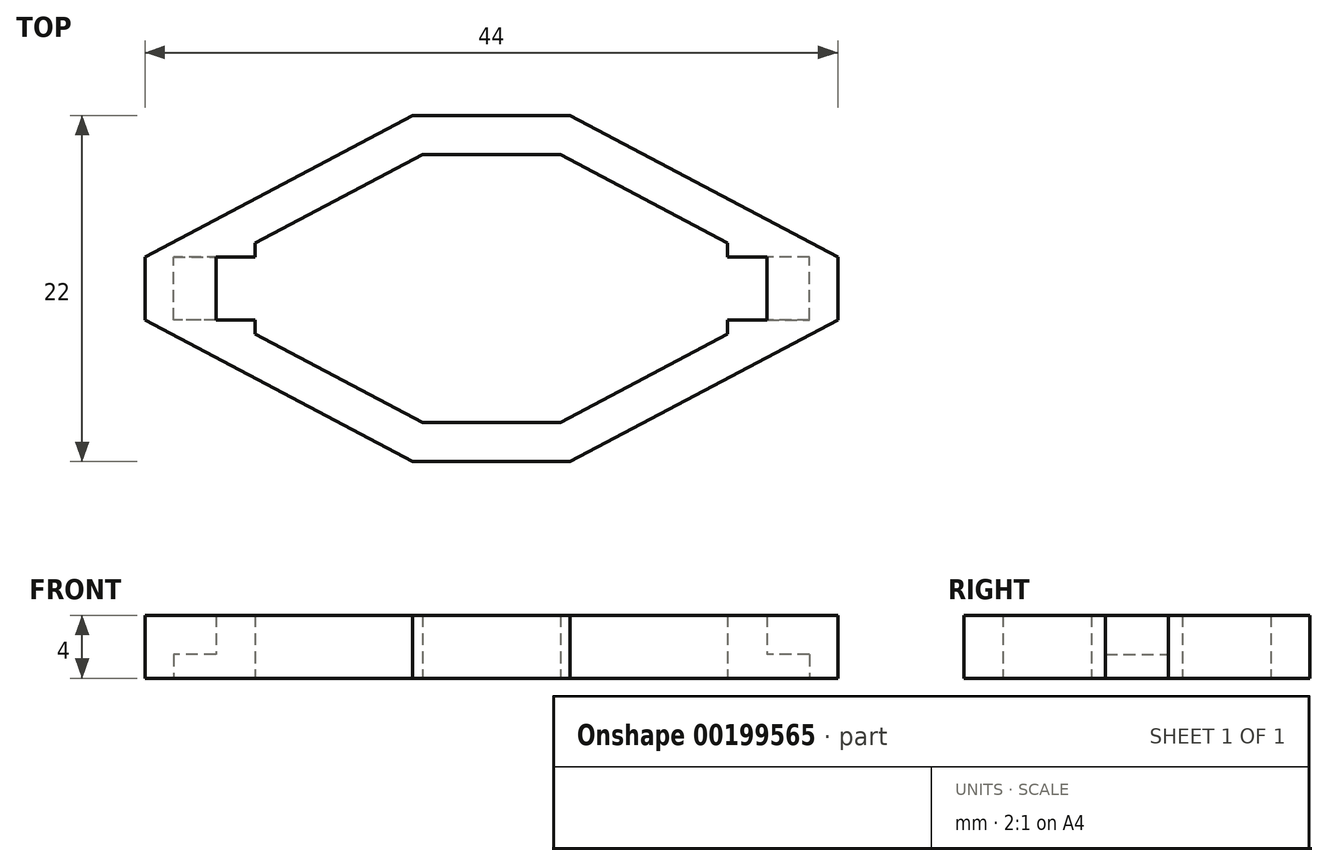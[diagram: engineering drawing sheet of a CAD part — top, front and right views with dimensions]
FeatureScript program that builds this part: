
annotation { "Feature Type Name" : "Feature", "Feature Type Description" : "" }
export const myFeature = defineFeature(function(context is Context, id is Id, definition is map)
    precondition{}
    {
        {
            var Q0;
            Q0=qCreatedBy(makeId("Top.planeOp"),FACE);
            var sketch = newSketch(context, id + "F0", { "sketchPlane" : qUnion([Q0])});
            skLineSegment(sketch, "E0.bottom", {"start": v(5, -11) * mm, "end": v(-5, -11) * mm});
            skLineSegment(sketch, "E0.top", {"start": v(5, 11) * mm, "end": v(-5, 11) * mm});
            skLineSegment(sketch, "E0.left", {"start": v(22, -2) * mm, "end": v(22, 2) * mm});
            skLineSegment(sketch, "E0.right", {"start": v(-22, -2) * mm, "end": v(-22, 2) * mm});
            skPoint(sketch, "E0.middle", {"position": v(0, 0) * mm});
            skLineSegment(sketch, "E1.bottom", {"start": v(4.38, -8.5) * mm, "end": v(-4.38, -8.5) * mm});
            skLineSegment(sketch, "E1.left", {"start": v(17.5, -2) * mm, "end": v(17.5, 2) * mm});
            skLineSegment(sketch, "E1.right", {"start": v(-17.5, -2) * mm, "end": v(-17.5, 2) * mm});
            skLineSegment(sketch, "E2.bottom", {"start": v(17.5, -2) * mm, "end": v(15, -2) * mm});
            skLineSegment(sketch, "E2.top", {"start": v(17.5, 2) * mm, "end": v(15, 2) * mm});
            skLineSegment(sketch, "E3", {"start": v(-22, 2) * mm, "end": v(-5, 11) * mm});
            skLineSegment(sketch, "E4", {"start": v(5, 11) * mm, "end": v(22, 2) * mm});
            skLineSegment(sketch, "E5", {"start": v(-22, -2) * mm, "end": v(-5, -11) * mm});
            skLineSegment(sketch, "E6", {"start": v(5, -11) * mm, "end": v(22, -2) * mm});
            skLineSegment(sketch, "E7", {"start": v(-15, 2.88) * mm, "end": v(-15, 2) * mm});
            skLineSegment(sketch, "E8", {"start": v(15, 2.88) * mm, "end": v(15, 2) * mm});
            skLineSegment(sketch, "E9.trimOffspring", {"start": v(4.38, 8.5) * mm, "end": v(-4.38, 8.5) * mm});
            skLineSegment(sketch, "E10.1", {"start": v(-15, -2.88) * mm, "end": v(-4.38, -8.5) * mm});
            skLineSegment(sketch, "E10.2", {"start": v(-15, 2.88) * mm, "end": v(-4.38, 8.5) * mm});
            skLineSegment(sketch, "E10.5", {"start": v(4.38, 8.5) * mm, "end": v(15, 2.88) * mm});
            skLineSegment(sketch, "E10.7", {"start": v(4.38, -8.5) * mm, "end": v(15, -2.88) * mm});
            skLineSegment(sketch, "E11.trimOffspring", {"start": v(-15, 2) * mm, "end": v(-17.5, 2) * mm});
            skLineSegment(sketch, "E12.trimOffspring", {"start": v(-15, -2) * mm, "end": v(-15, -2.88) * mm});
            skLineSegment(sketch, "E13.trimOffspring", {"start": v(-15, -2) * mm, "end": v(-17.5, -2) * mm});
            skLineSegment(sketch, "E14.trimOffspring", {"start": v(15, -2) * mm, "end": v(15, -2.88) * mm});
            skPoint(sketch, "E15", {"position": v(-22, 2) * mm});
            skPoint(sketch, "E16", {"position": v(-17.5, 2) * mm});
            skPoint(sketch, "E17", {"position": v(-17.5, -2) * mm});
            skPoint(sketch, "E18", {"position": v(-22, -2) * mm});
            skPoint(sketch, "E19", {"position": v(17.5, 2) * mm});
            skPoint(sketch, "E20", {"position": v(22, 2) * mm});
            skPoint(sketch, "E21", {"position": v(17.5, -2) * mm});
            skPoint(sketch, "E22", {"position": v(22, -2) * mm});
            skSolve(sketch);
        }
        {
            var Q0;
            Q0=makeQuery(id+"F0.imprint","IMPRINT",FACE,{"disambiguationData":[TD([[makeQuery(id+"F0.imprint","IMPRINT",EDGE,{"derivedFrom":sQuery(id+"F0.wireOp",EDGE,"E1.left")}),-1.0]])]});
            extrude(context, id + "F1", {"entities" : qUnion([Q0]), "depth" : 4 * mm});
        }
        {
            var Q0;
            Q0=makeQuery(id+"F1.opExtrude","CAP_FACE",FACE,{"disambiguationData":[OSD([sQuery(id+"F0.wireOp",EDGE,"E1.left"),sQuery(id+"F0.wireOp",EDGE,"E1.right"),sQuery(id+"F0.wireOp",EDGE,"E2.bottom"),sQuery(id+"F0.wireOp",EDGE,"E2.top"),sQuery(id+"F0.wireOp",EDGE,"E0.left"),sQuery(id+"F0.wireOp",EDGE,"E0.right"),sQuery(id+"F0.wireOp",EDGE,"E0.bottom"),sQuery(id+"F0.wireOp",EDGE,"E0.top"),sQuery(id+"F0.wireOp",EDGE,"E3"),sQuery(id+"F0.wireOp",EDGE,"E4"),sQuery(id+"F0.wireOp",EDGE,"E5"),sQuery(id+"F0.wireOp",EDGE,"E6"),sQuery(id+"F0.wireOp",EDGE,"E7"),sQuery(id+"F0.wireOp",EDGE,"E8"),sQuery(id+"F0.wireOp",EDGE,"E10.1"),sQuery(id+"F0.wireOp",EDGE,"E10.2"),sQuery(id+"F0.wireOp",EDGE,"E1.bottom"),sQuery(id+"F0.wireOp",EDGE,"E9.trimOffspring"),sQuery(id+"F0.wireOp",EDGE,"E10.5"),sQuery(id+"F0.wireOp",EDGE,"E10.7"),sQuery(id+"F0.wireOp",EDGE,"E11.trimOffspring"),sQuery(id+"F0.wireOp",EDGE,"E12.trimOffspring"),sQuery(id+"F0.wireOp",EDGE,"E13.trimOffspring"),sQuery(id+"F0.wireOp",EDGE,"E14.trimOffspring")])],"isStart":true});
            var sketch = newSketch(context, id + "F2", { "sketchPlane" : qUnion([Q0])});
            skLineSegment(sketch, "E23", {"start": v(-17.5, 2) * mm, "end": v(-22, 2) * mm});
            skLineSegment(sketch, "E24", {"start": v(-22, 2) * mm, "end": v(-22, -2) * mm});
            skLineSegment(sketch, "E25", {"start": v(-22, -2) * mm, "end": v(-17.5, -2) * mm});
            skLineSegment(sketch, "E26", {"start": v(-17.5, -2) * mm, "end": v(-17.5, 2) * mm});
            skLineSegment(sketch, "E27", {"start": v(17.5, 2) * mm, "end": v(22, 2) * mm});
            skLineSegment(sketch, "E28", {"start": v(22, 2) * mm, "end": v(22, -2) * mm});
            skLineSegment(sketch, "E29", {"start": v(22, -2) * mm, "end": v(17.5, -2) * mm});
            skLineSegment(sketch, "E30", {"start": v(17.5, -2) * mm, "end": v(17.5, 2) * mm});
            skLineSegment(sketch, "E31", {"start": v(-20.2, 2) * mm, "end": v(-20.2, -2) * mm});
            skLineSegment(sketch, "E32", {"start": v(20.2, 2) * mm, "end": v(20.2, -2) * mm});
            skSolve(sketch);
        }
        {
            var Q0;
            {var subQ0=sQuery(id+"F2.wireOp",EDGE,"E26");Q0=makeQuery(id+"F2.imprint","IMPRINT",FACE,{"disambiguationData":[TD([[makeQuery(id+"F2.imprint","IMPRINT",EDGE,{"derivedFrom":subQ0}),-1.0]])]});}
            var Q1;
            {var subQ0=sQuery(id+"F2.wireOp",EDGE,"E30");Q1=makeQuery(id+"F2.imprint","IMPRINT",FACE,{"disambiguationData":[TD([[makeQuery(id+"F2.imprint","IMPRINT",EDGE,{"derivedFrom":subQ0}),1.0]])]});}
            extrude(context, id + "F3", {"entities" : qUnion([Q0, Q1]), "operationType" : NewBodyOperationType.REMOVE, "oppositeDirection" : true, "depth" : 1.5 * mm});
        }
    });
